# Revit family: 002_Hand-Wash-Sink_Haws-Corporation_Wall-Mounted_7660
name_source: partatom
category: Plumbing Fixtures
units: mm (PartAtom-declared; Revit-internal decimal feet)

## family parameters
Cut with Voids When Loaded = No
Host = Face
OmniClass Number = 23.45.05.14
OmniClass Title = Plumbing Fixtures - Sanitary Washing Units
Part Type = Normal
Room Calculation Point = No
Round Connector Dimension = Use Radius
Shared = No

## types (1)
- 7660
    Apparent Load = 0 VA
    CW Connection = Yes
    CWFU = 1
    Default Elevation = 10"
    Depth = 20"
    Description = Model 7660 hand wash sink with eye and face wash features the medically acclaimed AXION MSR eye/face wash head assembly. This revolutionary inverted flow design is the only product on the market that provides a Medically Superior Response consistent with all EMT, emergency room and doctors' office protocols by sweeping contaminants away from the vulnerable nasal cavity. Traditional eyewashes irrigate from the outside edge of the eye back toward the nose, where contaminants can then be flushed into the nasal cavity through the lacrimal punctum, nature's ocular cavity drain.
    Flow = 4 GPM
    HW Connection = Yes
    HWFU = 1
    Height = 26 3/8"
    Housing Material = Haws Corporation - Metal - Stainless Steel
    Manufacturer = Haws Corporation
    Model = 7660
    Number of Poles = 1
    Power Consumption = 0 W
    Power Factor = 1
    Product Documentation Link = https://www.hawsco.com
    Product Page URL = https://www.hawsco.com
    Product data url = https://www.bimobject.com
    Sanitary Radius = 3/4"
    Supply Radius = 1/4"
    URL = https://www.hawsco.com
    Vent Connection = Yes
    Voltage = 120 V
    WFU = 1
    Waste Connection = Yes
    Width = 24"

## geometry (parser evidence)
native form markers: Blend x2, Sweep x3
no freeform markers — native parametric forms only
